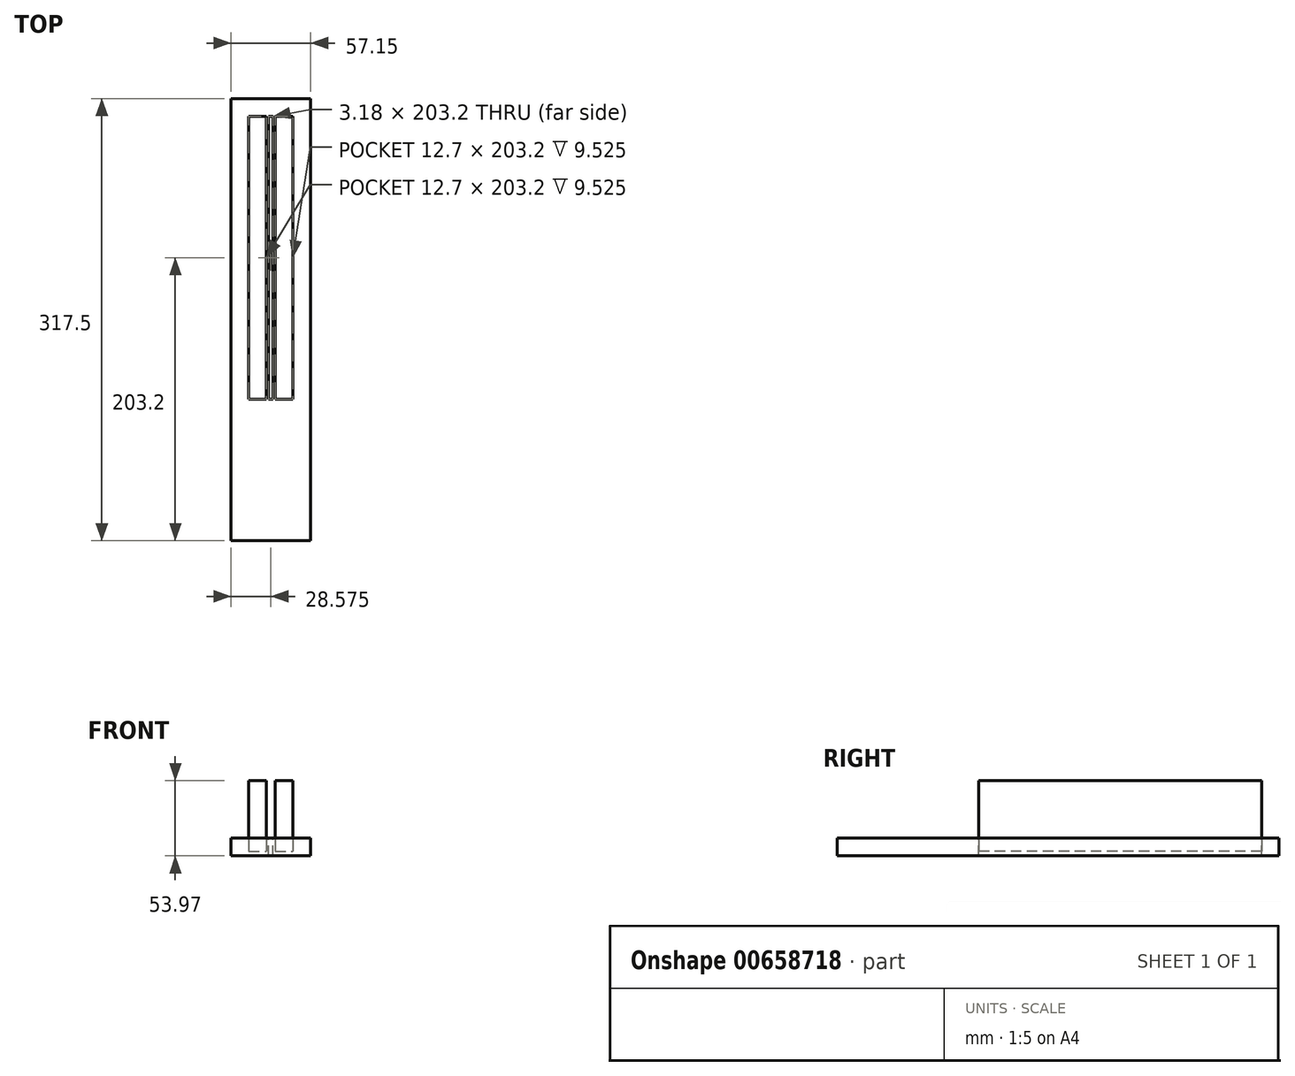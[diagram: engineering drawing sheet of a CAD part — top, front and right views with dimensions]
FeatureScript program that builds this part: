
annotation { "Feature Type Name" : "Feature", "Feature Type Description" : "" }
export const myFeature = defineFeature(function(context is Context, id is Id, definition is map)
    precondition{}
    {
        {
            var Q0;
            Q0=qCreatedBy(makeId("Top.planeOp"),FACE);
            var sketch = newSketch(context, id + "F0", { "sketchPlane" : qUnion([Q0])});
            skLineSegment(sketch, "E0.bottom", {"start": v(0, 317.5) * mm, "end": v(-57.15, 317.5) * mm});
            skLineSegment(sketch, "E0.top", {"start": v(0, 0) * mm, "end": v(-57.15, 0) * mm});
            skLineSegment(sketch, "E0.left", {"start": v(0, 317.5) * mm, "end": v(0, 0) * mm});
            skLineSegment(sketch, "E0.right", {"start": v(-57.15, 317.5) * mm, "end": v(-57.15, 0) * mm});
            skLineSegment(sketch, "E1.top", {"start": v(-44.45, 101.6) * mm, "end": v(-31.75, 101.6) * mm});
            skLineSegment(sketch, "E1.left", {"start": v(-44.45, 304.8) * mm, "end": v(-44.45, 101.6) * mm});
            skLineSegment(sketch, "E1.right", {"start": v(-31.75, 304.8) * mm, "end": v(-31.75, 101.6) * mm});
            skLineSegment(sketch, "E2.top", {"start": v(-25.4, 101.6) * mm, "end": v(-12.7, 101.6) * mm});
            skLineSegment(sketch, "E2.left", {"start": v(-25.4, 304.8) * mm, "end": v(-25.4, 101.6) * mm});
            skLineSegment(sketch, "E2.right", {"start": v(-12.7, 304.8) * mm, "end": v(-12.7, 101.6) * mm});
            skLineSegment(sketch, "E3", {"start": v(-31.75, 304.8) * mm, "end": v(-44.45, 304.8) * mm});
            skLineSegment(sketch, "E4", {"start": v(-25.4, 304.8) * mm, "end": v(-12.7, 304.8) * mm});
            skLineSegment(sketch, "E5", {"start": v(-31.75, 304.8) * mm, "end": v(-25.4, 304.8) * mm});
            skLineSegment(sketch, "E6", {"start": v(-31.75, 101.6) * mm, "end": v(-25.4, 101.6) * mm});
            skLineSegment(sketch, "E7.bottom", {"start": v(-30.16, 101.6) * mm, "end": v(-26.99, 101.6) * mm});
            skLineSegment(sketch, "E7.top", {"start": v(-30.16, 304.8) * mm, "end": v(-26.99, 304.8) * mm});
            skLineSegment(sketch, "E7.left", {"start": v(-30.16, 101.6) * mm, "end": v(-30.16, 304.8) * mm});
            skLineSegment(sketch, "E7.right", {"start": v(-26.99, 101.6) * mm, "end": v(-26.99, 304.8) * mm});
            skPoint(sketch, "E8", {"position": v(-28.57, 304.8) * mm});
            skPoint(sketch, "E9", {"position": v(-28.58, 304.8) * mm});
            skSolve(sketch);
        }
        {
            var Q0;
            Q0 = qSketchRegion(id + "F0", true);
            var Q1;
            Q1=makeQuery(id+"F0.imprint","IMPRINT",FACE,{"disambiguationData":[TD([[makeQuery(id+"F0.imprint","IMPRINT",EDGE,{"derivedFrom":sQuery(id+"F0.wireOp",EDGE,"E2.top")}),1.0]])]});
            var Q2;
            Q2=makeQuery(id+"F0.imprint","IMPRINT",FACE,{"disambiguationData":[TD([[makeQuery(id+"F0.imprint","IMPRINT",EDGE,{"derivedFrom":sQuery(id+"F0.wireOp",EDGE,"E1.right")}),1.0]])]});
            var Q3;
            Q3=makeQuery(id+"F0.imprint","IMPRINT",FACE,{"disambiguationData":[TD([[makeQuery(id+"F0.imprint","IMPRINT",EDGE,{"derivedFrom":sQuery(id+"F0.wireOp",EDGE,"E1.top")}),1.0]])]});
            var Q4;
            Q4=makeQuery(id+"F0.imprint","IMPRINT",FACE,{"disambiguationData":[TD([[makeQuery(id+"F0.imprint","IMPRINT",EDGE,{"derivedFrom":sQuery(id+"F0.wireOp",EDGE,"E7.bottom")}),1.0]])]});
            var Q5;
            {var subQ0=sQuery(id+"F0.wireOp",EDGE,"E2.left");Q5=makeQuery(id+"F0.imprint","IMPRINT",FACE,{"disambiguationData":[TD([[makeQuery(id+"F0.imprint","IMPRINT",EDGE,{"derivedFrom":subQ0}),-1.0]])]});}
            extrude(context, id + "F1", {"entities" : qUnion([Q0, Q1, Q2, Q3, Q4, Q5]), "oppositeDirection" : true, "depth" : 12.7 * mm, "offsetDistance" : 25.4 * mm});
        }
        {
            var Q0;
            Q0=makeQuery(id+"F0.imprint","IMPRINT",FACE,{"disambiguationData":[TD([[makeQuery(id+"F0.imprint","IMPRINT",EDGE,{"derivedFrom":sQuery(id+"F0.wireOp",EDGE,"E1.top")}),1.0]])]});
            var Q1;
            Q1=makeQuery(id+"F0.imprint","IMPRINT",FACE,{"disambiguationData":[TD([[makeQuery(id+"F0.imprint","IMPRINT",EDGE,{"derivedFrom":sQuery(id+"F0.wireOp",EDGE,"E2.top")}),1.0]])]});
            extrude(context, id + "F2", {"entities" : qUnion([Q0, Q1]), "operationType" : NewBodyOperationType.REMOVE, "oppositeDirection" : true, "depth" : 9.52 * mm, "offsetDistance" : 25.4 * mm});
        }
        {
            var Q0;
            Q0=makeQuery(id+"F2.boolean.opBoolean","COPY",FACE,{"derivedFrom":makeQuery(id+"F2.opExtrude","CAP_FACE",FACE,{"disambiguationData":[OSD([sQuery(id+"F0.wireOp",EDGE,"E1.top"),sQuery(id+"F0.wireOp",EDGE,"E1.left"),sQuery(id+"F0.wireOp",EDGE,"E1.right"),sQuery(id+"F0.wireOp",EDGE,"E3")])],"isStart":false})});
            var Q1;
            Q1=makeQuery(id+"F2.boolean.opBoolean","COPY",FACE,{"derivedFrom":makeQuery(id+"F2.opExtrude","CAP_FACE",FACE,{"disambiguationData":[OSD([sQuery(id+"F0.wireOp",EDGE,"E2.top"),sQuery(id+"F0.wireOp",EDGE,"E2.left"),sQuery(id+"F0.wireOp",EDGE,"E2.right"),sQuery(id+"F0.wireOp",EDGE,"E4")])],"isStart":false})});
            extrude(context, id + "F3", {"entities" : qUnion([Q0, Q1]), "depth" : 50.8 * mm, "offsetDistance" : 25.4 * mm});
        }
    });
